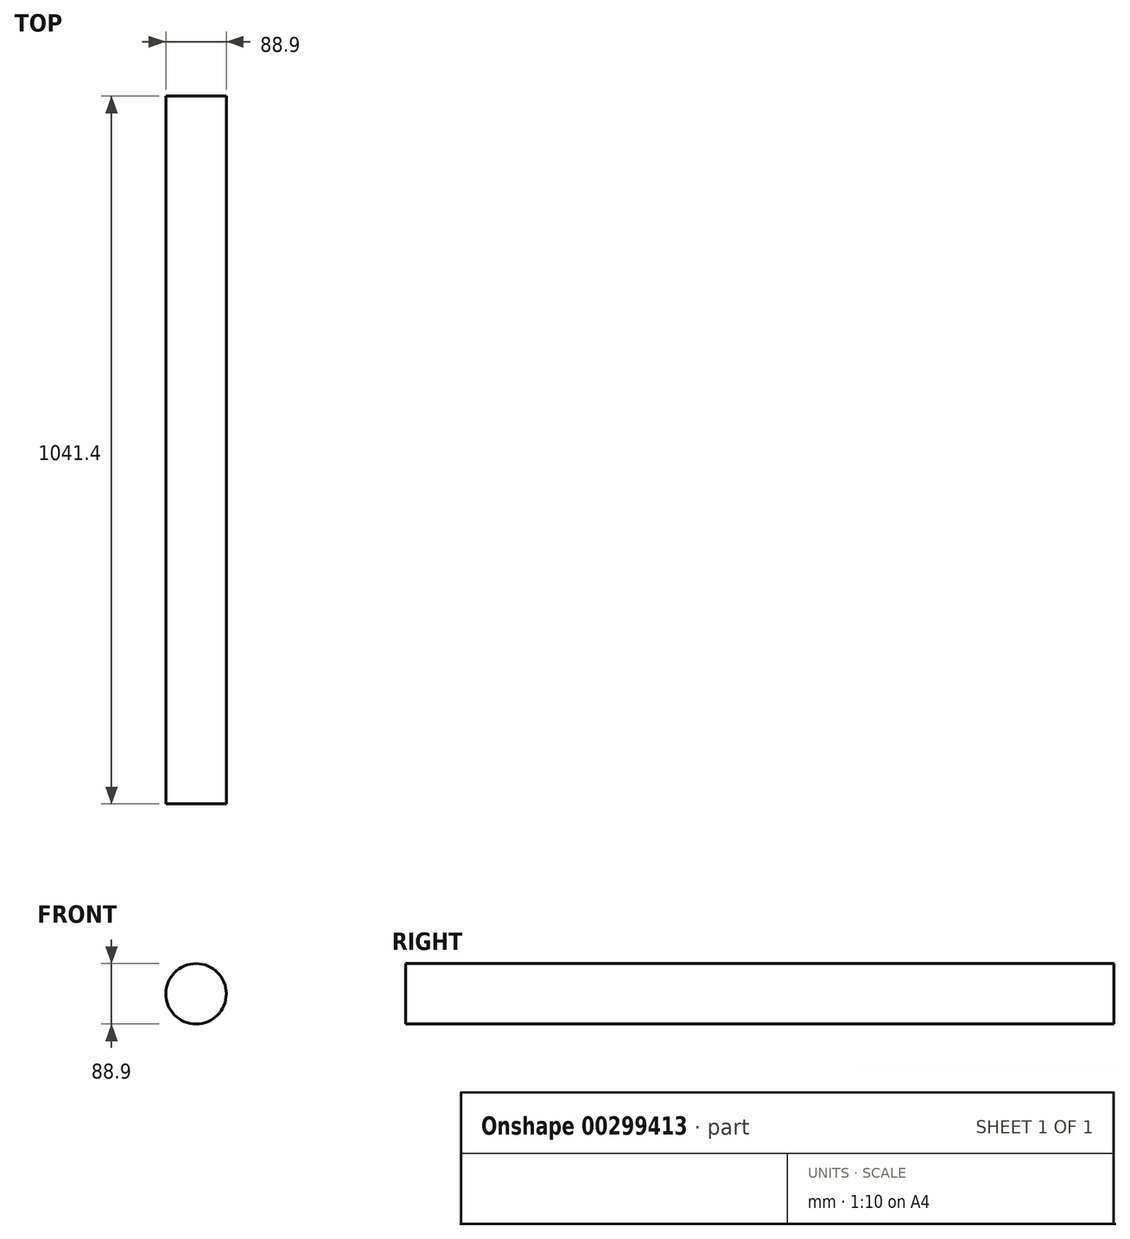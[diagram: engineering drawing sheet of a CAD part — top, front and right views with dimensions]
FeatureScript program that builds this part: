
annotation { "Feature Type Name" : "Feature", "Feature Type Description" : "" }
export const myFeature = defineFeature(function(context is Context, id is Id, definition is map)
    precondition{}
    {
        {
            var Q0;
            Q0=qCreatedBy(makeId("Front.planeOp"),FACE);
            var sketch = newSketch(context, id + "F0", { "sketchPlane" : qUnion([Q0])});
            skCircle(sketch, "E0", {"center": v(0, 0) * mm, "radius": 44.45 * mm});
            skSolve(sketch);
        }
        {
            var Q0;
            Q0 = qSketchRegion(id + "F0", true);
            extrude(context, id + "F1", {"entities" : qUnion([Q0]), "depth" : 1041.4 * mm});
        }
    });
